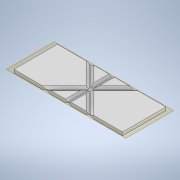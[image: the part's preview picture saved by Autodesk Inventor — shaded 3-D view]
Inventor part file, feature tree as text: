
AUTODESK INVENTOR PART (.ipt)
format: ipt  version: 2020 (Build 240168000, 168)  size: 244,736 bytes
history: native  units: mm
features: chamfer x24, projected_geometry x6, extrude x2, sketch x2, plane x1
ambient origin geometry x8: Origin, YZ Plane, XZ Plane, XY Plane, X Axis, Y Axis, Z Axis, Center Point
bodies: Solid1 (feature_tree)
feature tree (35):
  extrude  "Extrusion1"  Depth=20.0mm
  plane  "Work Plane1"
  extrude  "Extrusion2"  Depth=0.605mm
  chamfer  "Chamfer1"  Distance=10.0mm
  chamfer  "Chamfer2"  Distance=10.0mm
  chamfer  "Chamfer3"  Distance=0.5mm
  chamfer  "Chamfer4"  Distance=25.0mm
  chamfer  "Chamfer5"  Distance=0.5mm
  chamfer  "Chamfer6"  Distance=50.0mm
  chamfer  "Chamfer7"  Distance=0.5mm
  chamfer  "Chamfer8"  Distance=50.0mm
  chamfer  "Chamfer9"  Distance=1.5mm
  chamfer  "Chamfer10"  Distance=0.29mm
  chamfer  "Chamfer11"  Distance=0.605mm Angle=60.0deg
  chamfer  "Chamfer12"  Distance=0.605mm Angle=60.0deg
  chamfer  "Chamfer13"  Distance=0.605mm Angle=60.0deg
  chamfer  "Chamfer14"  Distance=0.605mm Angle=60.0deg
  chamfer  "Chamfer15"  Distance=0.605mm Angle=60.0deg
  chamfer  "Chamfer16"  Distance=0.605mm Angle=60.0deg
  chamfer  "Chamfer17"  Distance=0.605mm Angle=60.0deg
  chamfer  "Chamfer18"  Distance=0.605mm Angle=60.0deg
  chamfer  "Chamfer19"  Distance=0.605mm Angle=60.0deg
  chamfer  "Chamfer20"  Distance=0.605mm Angle=60.0deg
  chamfer  "Chamfer21"  Distance=0.605mm Angle=60.0deg
  chamfer  "Chamfer22"  Distance=0.605mm Angle=60.0deg
  chamfer  "Chamfer23"  Distance=0.605mm Angle=60.0deg
  chamfer  "Chamfer24"  Distance=0.605mm Angle=60.0deg
  sketch  "Sketch1"  dims[d0=50.0mm d1=20.0mm]
  sketch  "Sketch2"  dims[d2=10.0mm d3=10.0mm d4=10.0mm d5=10.0mm d6=0.5mm d7=25.0mm d8=0.5mm d9=50.0mm d10=0.5mm d11=50.0mm d12=1.5mm d13=0.0mm d14=0.29mm d15=0.0mm d16=1.0mm d17=0.605mm d18=60.0deg d19=1.0mm d20=0.605mm d21=60.0deg d22=1.0mm d23=0.605mm d24=60.0deg d25=1.0mm d26=0.605mm d27=60.0deg d28=1.0mm d29=0.605mm d30=60.0deg d31=1.0mm d32=0.605mm d33=60.0deg d34=1.0mm d35=0.605mm d36=60.0deg d37=1.0mm d38=0.605mm d39=60.0deg d40=1.0mm d41=0.605mm d42=60.0deg d43=1.0mm d44=0.605mm d45=60.0deg d46=1.0mm d47=0.605mm d48=60.0deg d49=1.0mm d50=0.605mm d51=60.0deg d52=0.605mm d53=1.0mm d54=60.0deg d55=0.605mm d56=1.0mm d57=60.0deg d58=0.605mm d59=1.0mm d60=60.0deg d61=0.605mm d62=1.0mm d63=60.0deg d64=0.605mm d65=1.0mm d66=60.0deg d67=0.605mm d68=1.0mm d69=60.0deg d70=0.605mm d71=1.0mm d72=60.0deg d73=0.605mm d74=1.0mm d75=60.0deg d76=0.605mm d77=1.0mm d78=60.0deg d79=0.605mm d80=1.0mm d81=60.0deg d82=0.605mm d83=1.0mm d84=60.0deg d85=0.605mm d86=1.0mm d87=60.0deg]
  projected_geometry  "Projected Loop1"
  projected_geometry  "Projected Loop2"
  projected_geometry  "Projected Loop3"
  projected_geometry  "Projected Loop4"
  projected_geometry  "Projected Loop5"
  projected_geometry  "Projected Loop6"
